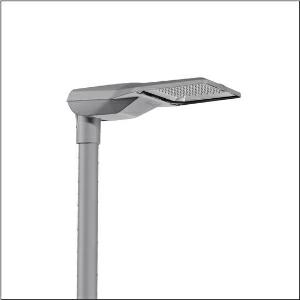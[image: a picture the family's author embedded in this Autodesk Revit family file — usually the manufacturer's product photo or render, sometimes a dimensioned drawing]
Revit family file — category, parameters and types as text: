
# Revit family: streetlight_sl_21_iq_midi___st1_0a_5xe3d31d08nb_3762
name_source: partatom
category: Lighting Fixtures
units: mm (PartAtom-declared; Revit-internal decimal feet)

## family parameters
Cut with Voids When Loaded = No
Host = Face
Light Source = No
Part Type = Normal
Room Calculation Point = No
Round Connector Dimension = Use Diameter
Shared = No

## types (1)
- --- (1 x LED, 23230 lm, 155.5 W, 3000K)
    Apparent Load = 155 VA
    CIE Flux Codes = 40 73 97 100 100
    Color Rendering = 70
    Color Temperature = 3000K
    Default Elevation = 1800 mm
    Description = Streetlight SL 21 iQ midi, mast luminaire, primary light control with lens, of PMMA, primary optical cover: cover, of toughened safety glass, transparent, light distribution: ST1.0a, light emission: direct distribution, primary light characteristic: asymmetric, installation type: post-top, side-entry, LED, High Power LED, rated luminous flux: 23.230lm, luminous efficacy: 149lm/W, light colour: 730, colour temperature: 3000K, control: Auto-Match, Temp-Guard, Lumen-Switch, Night-Set, Smart-Wire, Light-Fading, Desk-Remote (wireless, voltage-free reading and setting of iQ features in the workshop via application-optimized NFC function/RFID function), optimised constant luminous flux control (CLO 2.0), presetting dimming linear, mains connection: 230..240V, AC, 50/60Hz, start of lifetime: 156W, end of service life: 162W, reduction: 69W, luminaire housing, of diecast aluminium, powder-coated, Siteco® metallic grey (DB 702S), corrosivity category C5 mid according to DIN EN ISO 12944, please order mast flange separately, inclination adjustable: 0°, 5°, 10°, 15°, sealing non-destructively replaceable, multi-level sealing system, length: 644mm, width: 335mm, height: 110mm, mast flange for spigot size: 42mm (side-entry): 5XC10008XM4, 60/48mm (side-entry/post-top): 5XC10108XM2, 76/60mm (side-entry/post-top): 5XC10108XM1, protection rating (complete): IP66, insulation class (complete): insulation class II (safety insulation), certification: CE, ENEC, ENEC+, VDE, impact resistance: IK09, permissible operating ambient temperature for outdoor applications: -40..+50°C, standard-compliant lighting for roads and squares, packaging unit: 1 piece

Light Distribution: ST1.0a
    Height = 111 mm
    Lamp = 1 x LED
    Lamp Light Flux = 23230 lm
    Lamp Power = 155.5 W
    Lamp count = 1
    Length = 644 mm
    Luminous efficacy = 149 lm/W
    Manufacturer = Siteco
    ModVariant = No
    Model = 5XE3D31D08NB
    Number of Poles = 1
    OnlyDefault = Yes
    Power Factor = 1
    Product Name = Streetlight SL 21 iQ midi | ST1.0a
    Product group = mast luminaire | pylon top
    ProductGroupID = 6100
    Protection Class = Protection class II
    Protection Degree = IP 66
    RLX_Detail_Level = 1
    RLX_Emergency_Light_Flux = 0 lm
    RLX_Emergency_Type = 0
    RLX_Emergency_Type_DB = No
    RlxData = <blob elided: 91413 chars, md5=f108a8c1>
    Socket = socket
    Standby Power = 0 W
    System Light Flux = 23230 lm
    System Power = 155 W
    Type Comments = factory setting: luminous flux: 100 % | dim-lin: 254 | 823 mA
    Type Image = l_1004298.jpg
    URL = http://relux.com
    VarID = @adj_121475
    Voltage = 0 V
    Weight = 0.00 kg
    Width = 336 mm

## geometry (parser evidence)
native form markers: Blend x4, Sweep x9
no freeform markers — native parametric forms only
